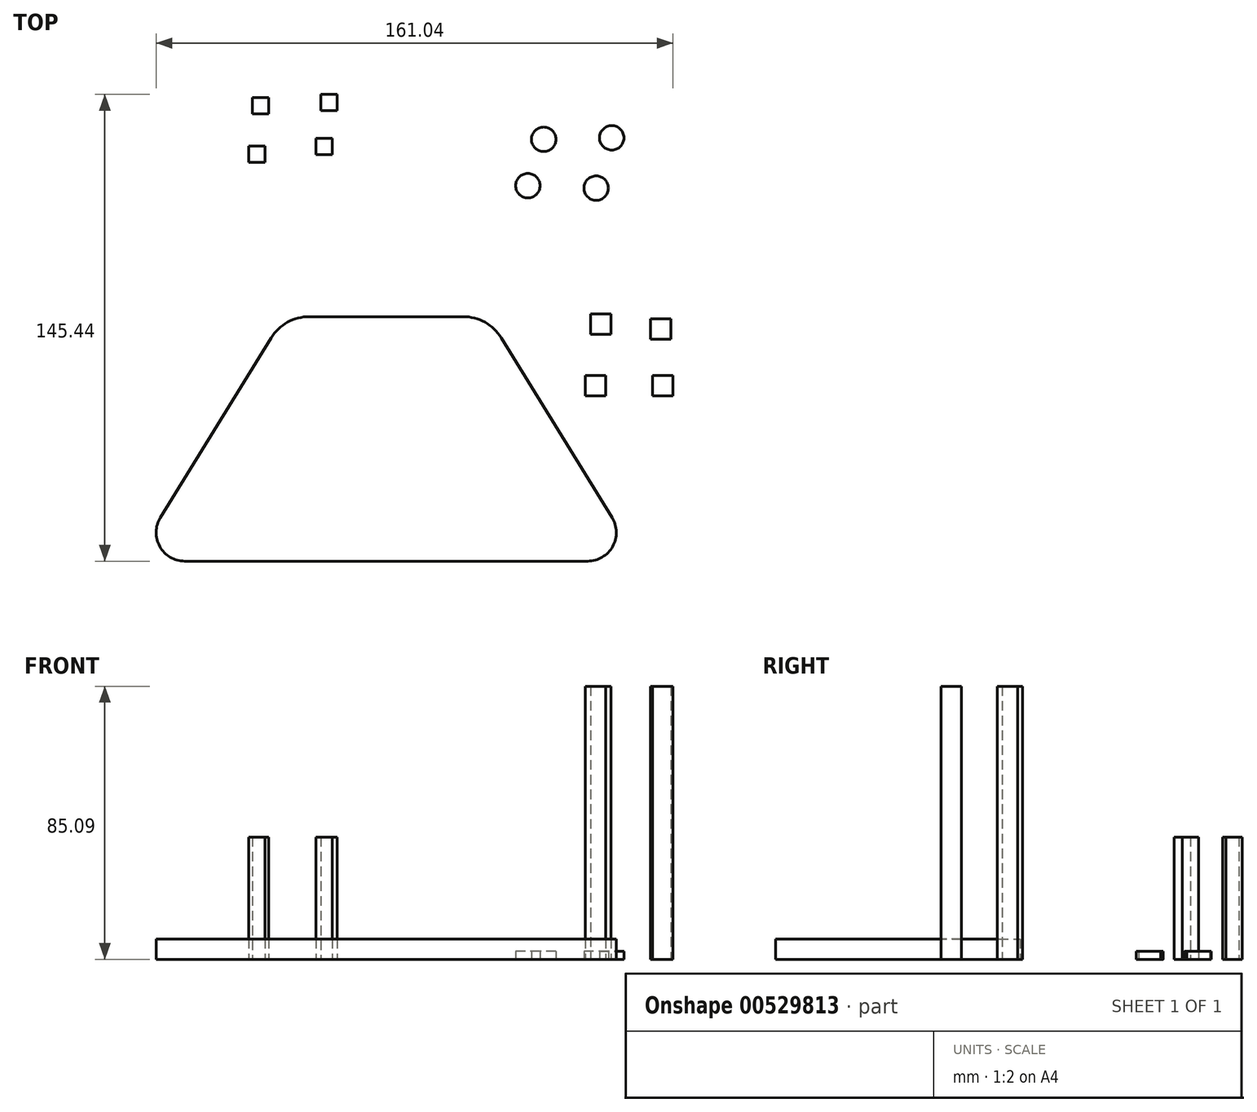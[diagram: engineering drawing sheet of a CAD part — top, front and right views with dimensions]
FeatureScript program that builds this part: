
annotation { "Feature Type Name" : "Feature", "Feature Type Description" : "" }
export const myFeature = defineFeature(function(context is Context, id is Id, definition is map)
    precondition{}
    {
        {
            var Q0;
            Q0=qCreatedBy(makeId("Top.planeOp"),FACE);
            var sketch = newSketch(context, id + "F0", { "sketchPlane" : qUnion([Q0])});
            skLineSegment(sketch, "E0.bottom", {"start": v(-55.7, 0) * mm, "end": v(-7.8, 0) * mm});
            skLineSegment(sketch, "E0.top", {"start": v(-63.5, -76.2) * mm, "end": v(0, -76.2) * mm});
            skLineSegment(sketch, "E0.left", {"start": v(-63.5, 0) * mm, "end": v(-63.5, -76.2) * mm});
            skLineSegment(sketch, "E0.right", {"start": v(0, 0) * mm, "end": v(0, -76.2) * mm});
            skLineSegment(sketch, "E1", {"start": v(0, -76.2) * mm, "end": v(31.06, -76.2) * mm});
            skLineSegment(sketch, "E2", {"start": v(-63.5, -76.2) * mm, "end": v(-94.56, -76.2) * mm});
            skLineSegment(sketch, "E3", {"start": v(-102.13, -62.64) * mm, "end": v(-67.6, -6.64) * mm});
            skLineSegment(sketch, "E4", {"start": v(4.1, -6.64) * mm, "end": v(38.63, -62.64) * mm});
            skPoint(sketch, "E5.visualSharp", {"position": v(-63.5, 0) * mm});
            skArc(sketch, "E5.filletArc", {"start": v(-55.7, 0) * mm, "mid": v(-62.51, -1.77) * mm, "end": v(-67.6, -6.64) * mm});
            skPoint(sketch, "E6.visualSharp", {"position": v(-110.5, -76.2) * mm});
            skArc(sketch, "E6.filletArc", {"start": v(-102.13, -62.64) * mm, "mid": v(-102.33, -71.64) * mm, "end": v(-94.56, -76.2) * mm});
            skPoint(sketch, "E7.visualSharp", {"position": v(47, -76.2) * mm});
            skArc(sketch, "E7.filletArc", {"start": v(31.06, -76.2) * mm, "mid": v(38.83, -71.64) * mm, "end": v(38.63, -62.64) * mm});
            skPoint(sketch, "E8.visualSharp", {"position": v(0, 0) * mm});
            skArc(sketch, "E8.filletArc", {"start": v(4.1, -6.64) * mm, "mid": v(-0.99, -1.77) * mm, "end": v(-7.8, 0) * mm});
            skSolve(sketch);
        }
        {
            var Q0;
            {var subQ4=sQuery(id+"F0.wireOp",EDGE,"E2");Q0=makeQuery(id+"F0.imprint","IMPRINT",FACE,{"disambiguationData":[TD([[makeQuery(id+"F0.imprint","IMPRINT",EDGE,{"derivedFrom":subQ4}),-1.0]])]});}
            var Q1;
            {var subQ7=sQuery(id+"F0.wireOp",EDGE,"E0.bottom");Q1=makeQuery(id+"F0.imprint","IMPRINT",FACE,{"disambiguationData":[TD([[makeQuery(id+"F0.imprint","IMPRINT",EDGE,{"derivedFrom":subQ7}),-1.0]])]});}
            var Q2;
            {var subQ1=sQuery(id+"F0.wireOp",EDGE,"E1");Q2=makeQuery(id+"F0.imprint","IMPRINT",FACE,{"disambiguationData":[TD([[makeQuery(id+"F0.imprint","IMPRINT",EDGE,{"derivedFrom":subQ1}),1.0]])]});}
            extrude(context, id + "F1", {"entities" : qUnion([Q0, Q1, Q2]), "depth" : 6.35 * mm, "offsetDistance" : 25.4 * mm});
        }
        {
            var Q0;
            Q0=qCreatedBy(makeId("Top.planeOp"),FACE);
            var sketch = newSketch(context, id + "F2", { "sketchPlane" : qUnion([Q0])});
            skLineSegment(sketch, "E9.bottom", {"start": v(38.36, -5.52) * mm, "end": v(32, -5.52) * mm});
            skLineSegment(sketch, "E9.top", {"start": v(38.36, 0.83) * mm, "end": v(32, 0.83) * mm});
            skLineSegment(sketch, "E9.left", {"start": v(38.36, -5.52) * mm, "end": v(38.36, 0.83) * mm});
            skLineSegment(sketch, "E9.right", {"start": v(32, -5.52) * mm, "end": v(32, 0.83) * mm});
            skPoint(sketch, "E9.middle", {"position": v(35.18, -2.34) * mm});
            skLineSegment(sketch, "E10.bottom", {"start": v(57, -0.69) * mm, "end": v(50.66, -0.69) * mm});
            skLineSegment(sketch, "E10.top", {"start": v(57, -7.04) * mm, "end": v(50.66, -7.04) * mm});
            skLineSegment(sketch, "E10.left", {"start": v(57, -0.69) * mm, "end": v(57, -7.04) * mm});
            skLineSegment(sketch, "E10.right", {"start": v(50.66, -0.69) * mm, "end": v(50.66, -7.04) * mm});
            skPoint(sketch, "E10.middle", {"position": v(53.83, -3.86) * mm});
            skLineSegment(sketch, "E11.bottom", {"start": v(36.7, -18.29) * mm, "end": v(30.35, -18.29) * mm});
            skLineSegment(sketch, "E11.top", {"start": v(36.7, -24.64) * mm, "end": v(30.35, -24.64) * mm});
            skLineSegment(sketch, "E11.left", {"start": v(36.7, -18.29) * mm, "end": v(36.7, -24.64) * mm});
            skLineSegment(sketch, "E11.right", {"start": v(30.35, -18.29) * mm, "end": v(30.35, -24.64) * mm});
            skPoint(sketch, "E11.middle", {"position": v(33.52, -21.46) * mm});
            skLineSegment(sketch, "E12.bottom", {"start": v(57.59, -18.29) * mm, "end": v(51.24, -18.29) * mm});
            skLineSegment(sketch, "E12.top", {"start": v(57.59, -24.64) * mm, "end": v(51.24, -24.64) * mm});
            skLineSegment(sketch, "E12.left", {"start": v(57.59, -18.29) * mm, "end": v(57.59, -24.64) * mm});
            skLineSegment(sketch, "E12.right", {"start": v(51.24, -18.29) * mm, "end": v(51.24, -24.64) * mm});
            skPoint(sketch, "E12.middle", {"position": v(54.41, -21.46) * mm});
            skSolve(sketch);
        }
        {
            var Q0;
            Q0=makeQuery(id+"F2.imprint","IMPRINT",FACE,{"disambiguationData":[TD([[makeQuery(id+"F2.imprint","IMPRINT",EDGE,{"derivedFrom":sQuery(id+"F2.wireOp",EDGE,"E9.bottom")}),-1.0]])]});
            var Q1;
            Q1=makeQuery(id+"F2.imprint","IMPRINT",FACE,{"disambiguationData":[TD([[makeQuery(id+"F2.imprint","IMPRINT",EDGE,{"derivedFrom":sQuery(id+"F2.wireOp",EDGE,"E10.bottom")}),1.0]])]});
            var Q2;
            Q2=makeQuery(id+"F2.imprint","IMPRINT",FACE,{"disambiguationData":[TD([[makeQuery(id+"F2.imprint","IMPRINT",EDGE,{"derivedFrom":sQuery(id+"F2.wireOp",EDGE,"E11.bottom")}),1.0]])]});
            var Q3;
            Q3=makeQuery(id+"F2.imprint","IMPRINT",FACE,{"disambiguationData":[TD([[makeQuery(id+"F2.imprint","IMPRINT",EDGE,{"derivedFrom":sQuery(id+"F2.wireOp",EDGE,"E12.bottom")}),1.0]])]});
            extrude(context, id + "F3", {"entities" : qUnion([Q0, Q1, Q2, Q3]), "depth" : 85.1 * mm, "offsetDistance" : 25.4 * mm});
        }
        {
            var Q0;
            Q0=qCreatedBy(makeId("Top.planeOp"),FACE);
            var sketch = newSketch(context, id + "F4", { "sketchPlane" : qUnion([Q0])});
            skLineSegment(sketch, "E13.bottom", {"start": v(-68.34, 63.2) * mm, "end": v(-73.42, 63.2) * mm});
            skLineSegment(sketch, "E13.top", {"start": v(-68.34, 68.27) * mm, "end": v(-73.42, 68.27) * mm});
            skLineSegment(sketch, "E13.left", {"start": v(-68.34, 63.2) * mm, "end": v(-68.34, 68.27) * mm});
            skLineSegment(sketch, "E13.right", {"start": v(-73.42, 63.2) * mm, "end": v(-73.42, 68.27) * mm});
            skPoint(sketch, "E13.middle", {"position": v(-70.88, 65.73) * mm});
            skLineSegment(sketch, "E14.bottom", {"start": v(-46.99, 64.16) * mm, "end": v(-52.07, 64.16) * mm});
            skLineSegment(sketch, "E14.top", {"start": v(-46.99, 69.24) * mm, "end": v(-52.07, 69.24) * mm});
            skLineSegment(sketch, "E14.left", {"start": v(-46.99, 64.16) * mm, "end": v(-46.99, 69.24) * mm});
            skLineSegment(sketch, "E14.right", {"start": v(-52.07, 64.16) * mm, "end": v(-52.07, 69.24) * mm});
            skPoint(sketch, "E14.middle", {"position": v(-49.53, 66.7) * mm});
            skLineSegment(sketch, "E15.bottom", {"start": v(-69.58, 48.07) * mm, "end": v(-74.66, 48.07) * mm});
            skLineSegment(sketch, "E15.top", {"start": v(-69.58, 53.15) * mm, "end": v(-74.66, 53.15) * mm});
            skLineSegment(sketch, "E15.left", {"start": v(-69.58, 48.07) * mm, "end": v(-69.58, 53.15) * mm});
            skLineSegment(sketch, "E15.right", {"start": v(-74.66, 48.07) * mm, "end": v(-74.66, 53.15) * mm});
            skPoint(sketch, "E15.middle", {"position": v(-72.12, 50.6) * mm});
            skLineSegment(sketch, "E16.bottom", {"start": v(-48.53, 50.54) * mm, "end": v(-53.61, 50.54) * mm});
            skLineSegment(sketch, "E16.top", {"start": v(-48.53, 55.62) * mm, "end": v(-53.61, 55.62) * mm});
            skLineSegment(sketch, "E16.left", {"start": v(-48.53, 50.54) * mm, "end": v(-48.53, 55.62) * mm});
            skLineSegment(sketch, "E16.right", {"start": v(-53.61, 50.54) * mm, "end": v(-53.61, 55.62) * mm});
            skPoint(sketch, "E16.middle", {"position": v(-51.07, 53.08) * mm});
            skSolve(sketch);
        }
        {
            var Q0;
            Q0=makeQuery(id+"F4.imprint","IMPRINT",FACE,{"disambiguationData":[TD([[makeQuery(id+"F4.imprint","IMPRINT",EDGE,{"derivedFrom":sQuery(id+"F4.wireOp",EDGE,"E15.bottom")}),-1.0]])]});
            var Q1;
            Q1=makeQuery(id+"F4.imprint","IMPRINT",FACE,{"disambiguationData":[TD([[makeQuery(id+"F4.imprint","IMPRINT",EDGE,{"derivedFrom":sQuery(id+"F4.wireOp",EDGE,"E16.bottom")}),-1.0]])]});
            var Q2;
            Q2=makeQuery(id+"F4.imprint","IMPRINT",FACE,{"disambiguationData":[TD([[makeQuery(id+"F4.imprint","IMPRINT",EDGE,{"derivedFrom":sQuery(id+"F4.wireOp",EDGE,"E13.bottom")}),-1.0]])]});
            var Q3;
            Q3=makeQuery(id+"F4.imprint","IMPRINT",FACE,{"disambiguationData":[TD([[makeQuery(id+"F4.imprint","IMPRINT",EDGE,{"derivedFrom":sQuery(id+"F4.wireOp",EDGE,"E14.bottom")}),-1.0]])]});
            extrude(context, id + "F5", {"entities" : qUnion([Q0, Q1, Q2, Q3]), "depth" : 38.1 * mm, "offsetDistance" : 25.4 * mm});
        }
        {
            var Q0;
            Q0=qCreatedBy(makeId("Top.planeOp"),FACE);
            var sketch = newSketch(context, id + "F6", { "sketchPlane" : qUnion([Q0])});
            skCircle(sketch, "E17", {"center": v(17.33, 55.25) * mm, "radius": 3.81 * mm});
            skCircle(sketch, "E18", {"center": v(38.53, 55.73) * mm, "radius": 3.81 * mm});
            skCircle(sketch, "E19", {"center": v(12.4, 40.79) * mm, "radius": 3.81 * mm});
            skCircle(sketch, "E20", {"center": v(33.68, 40.04) * mm, "radius": 3.81 * mm});
            skSolve(sketch);
        }
        {
            var Q0;
            Q0=makeQuery(id+"F6.imprint","IMPRINT",FACE,{"disambiguationData":[TD([[makeQuery(id+"F6.imprint","IMPRINT",EDGE,{"derivedFrom":sQuery(id+"F6.wireOp",EDGE,"E18")}),1.0]])]});
            var Q1;
            Q1=makeQuery(id+"F6.imprint","IMPRINT",FACE,{"disambiguationData":[TD([[makeQuery(id+"F6.imprint","IMPRINT",EDGE,{"derivedFrom":sQuery(id+"F6.wireOp",EDGE,"E19")}),1.0]])]});
            var Q2;
            Q2=makeQuery(id+"F6.imprint","IMPRINT",FACE,{"disambiguationData":[TD([[makeQuery(id+"F6.imprint","IMPRINT",EDGE,{"derivedFrom":sQuery(id+"F6.wireOp",EDGE,"E20")}),1.0]])]});
            var Q3;
            Q3=makeQuery(id+"F6.imprint","IMPRINT",FACE,{"disambiguationData":[TD([[makeQuery(id+"F6.imprint","IMPRINT",EDGE,{"derivedFrom":sQuery(id+"F6.wireOp",EDGE,"E17")}),1.0]])]});
            extrude(context, id + "F7", {"entities" : qUnion([Q0, Q1, Q2, Q3]), "depth" : 2.54 * mm, "offsetDistance" : 25.4 * mm});
        }
    });
